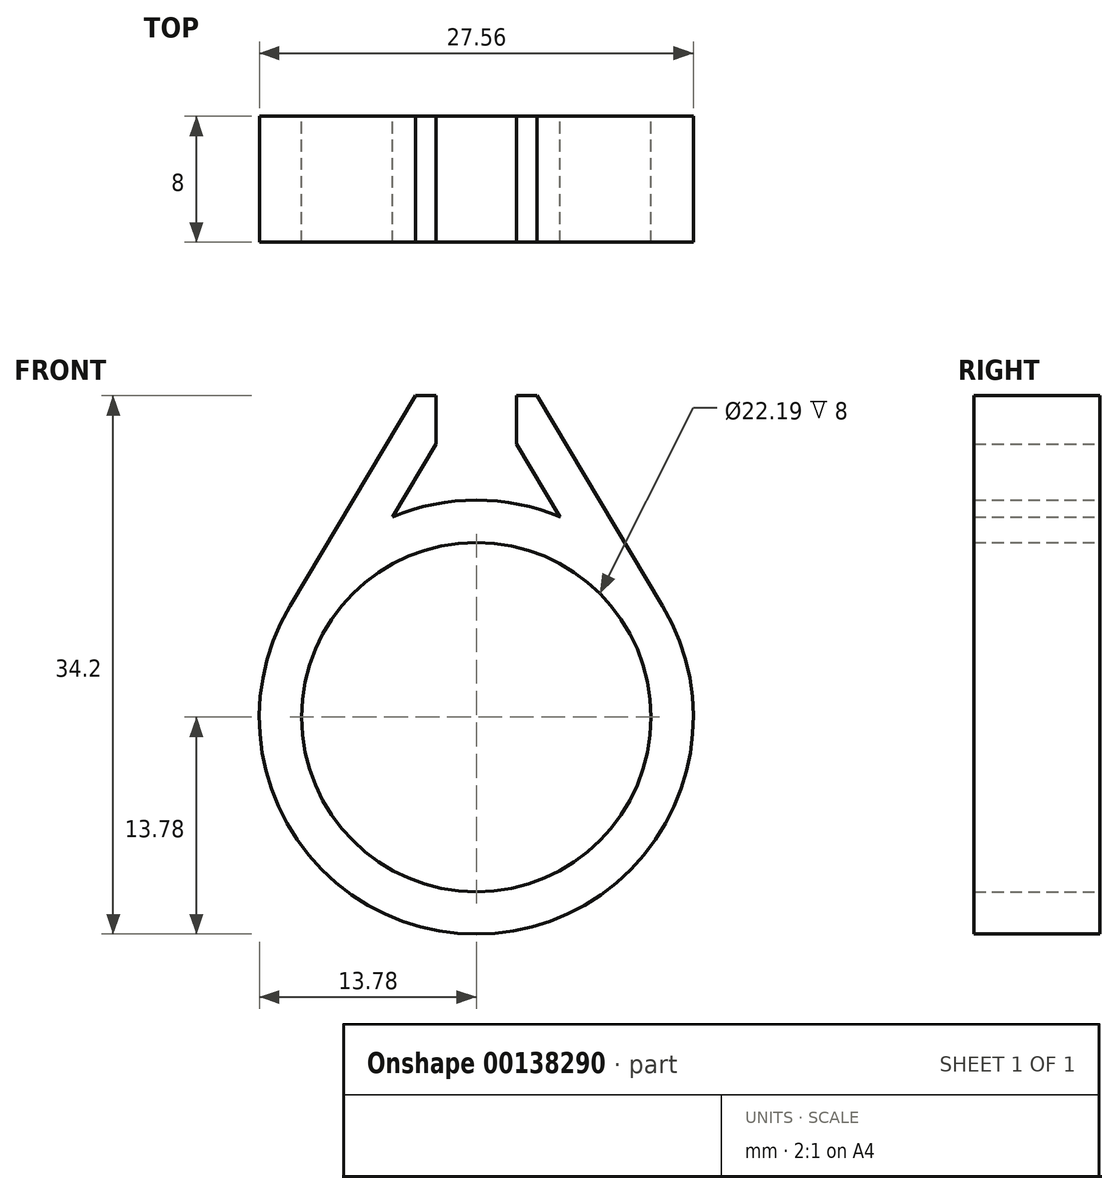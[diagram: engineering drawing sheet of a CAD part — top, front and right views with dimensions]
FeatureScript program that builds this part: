
annotation { "Feature Type Name" : "Feature", "Feature Type Description" : "" }
export const myFeature = defineFeature(function(context is Context, id is Id, definition is map)
    precondition{}
    {
        {
            var Q0;
            Q0=qCreatedBy(makeId("Front.planeOp"),FACE);
            var sketch = newSketch(context, id + "F0", { "sketchPlane" : qUnion([Q0])});
            skCircle(sketch, "E0", {"center": v(0, 0) * mm, "radius": 11.1 * mm});
            skCircle(sketch, "E1", {"center": v(0, 0) * mm, "radius": 13.78 * mm});
            skLineSegment(sketch, "E2.left", {"start": v(-2.56, 22.6) * mm, "end": v(-2.56, 17.72) * mm});
            skLineSegment(sketch, "E2.right", {"start": v(2.84, 22.6) * mm, "end": v(2.84, 17.22) * mm});
            skLineSegment(sketch, "E3", {"start": v(-2.56, 22.6) * mm, "end": v(-11.83, 7.07) * mm});
            skLineSegment(sketch, "E4", {"start": v(2.84, 22.6) * mm, "end": v(11.83, 7.07) * mm});
            skPoint(sketch, "E5.startSnap0", {"position": v(-7.2, 14.83) * mm});
            skPoint(sketch, "E6.endSnap0", {"position": v(7.34, 14.83) * mm});
            skPoint(sketch, "E7.orphan", {"position": v(-2.56, 25.36) * mm});
            skPoint(sketch, "E8.orphan", {"position": v(2.84, 24.86) * mm});
            skPoint(sketch, "E2.top.end.orphan", {"position": v(2.56, -25.36) * mm});
            skPoint(sketch, "E2.top.start.orphan", {"position": v(-2.84, -24.86) * mm});
            skPoint(sketch, "E5.start.orphan", {"position": v(-7.2, 11.75) * mm});
            skPoint(sketch, "E6.end.orphan", {"position": v(7.34, 12.29) * mm});
            skLineSegment(sketch, "E9", {"start": v(-2.56, 17.35) * mm, "end": v(-5.33, 12.71) * mm});
            skLineSegment(sketch, "E10", {"start": v(-5.33, 12.71) * mm, "end": v(-2.56, 17.35) * mm});
            skLineSegment(sketch, "E11", {"start": v(-2.56, 17.72) * mm, "end": v(-2.56, 17.35) * mm});
            skLineSegment(sketch, "E12.MirrorCS", {"start": v(2.56, 22.6) * mm, "end": v(2.56, 17.72) * mm});
            skLineSegment(sketch, "E13.MirrorCS", {"start": v(5.33, 12.71) * mm, "end": v(2.56, 17.35) * mm});
            skLineSegment(sketch, "E14.MirrorCS", {"start": v(2.56, 22.6) * mm, "end": v(11.83, 7.07) * mm});
            skLineSegment(sketch, "E15.MirrorCS", {"start": v(2.56, 17.72) * mm, "end": v(2.56, 17.35) * mm});
            skSolve(sketch);
        }
        {
            var Q0;
            Q0 = qSketchRegion(id + "F0", true);
            extrude(context, id + "F1", {"entities" : qUnion([Q0]), "depth" : 8 * mm});
        }
        {
            var Q0;
            Q0=makeQuery(id+"F1.opExtrude","CAP_FACE",FACE,{"disambiguationData":[OSD([sQuery(id+"F0.wireOp",EDGE,"E0"),sQuery(id+"F0.wireOp",EDGE,"E2.left"),sQuery(id+"F0.wireOp",EDGE,"E3"),sQuery(id+"F0.wireOp",EDGE,"E10"),sQuery(id+"F0.wireOp",EDGE,"E11"),sQuery(id+"F0.wireOp",EDGE,"E12.MirrorCS"),sQuery(id+"F0.wireOp",EDGE,"E13.MirrorCS"),sQuery(id+"F0.wireOp",EDGE,"E14.MirrorCS"),sQuery(id+"F0.wireOp",EDGE,"E1"),sQuery(id+"F0.wireOp",EDGE,"E15.MirrorCS")])],"isStart":false});
            var sketch = newSketch(context, id + "F2", { "sketchPlane" : qUnion([Q0])});
            skLineSegment(sketch, "E16.bottom", {"start": v(-6.74, 20.42) * mm, "end": v(10.76, 20.42) * mm});
            skLineSegment(sketch, "E16.top", {"start": v(-6.74, 23.38) * mm, "end": v(10.76, 23.38) * mm});
            skLineSegment(sketch, "E16.left", {"start": v(-6.74, 20.42) * mm, "end": v(-6.74, 23.38) * mm});
            skLineSegment(sketch, "E16.right", {"start": v(10.76, 20.42) * mm, "end": v(10.76, 23.38) * mm});
            skSolve(sketch);
        }
        {
            var Q0;
            {var subQ0=sQuery(id+"F2.wireOp",EDGE,"E16.bottom");var subQ1=makeQuery(id+"F1.opExtrude","CAP_EDGE",EDGE,{"disambiguationData":[OSD([sQuery(id+"F0.wireOp",EDGE,"E14.MirrorCS")])],"isStart":false});var subQ2=makeQuery(id+"F2.imprint","INTERSECT",VERTEX,{"derivedFrom":[subQ1,subQ0]});Q0=makeQuery(id+"F2.imprint","IMPRINT",FACE,{"disambiguationData":[TD([[makeQuery(id+"F2.imprint","IMPRINT",EDGE,{"disambiguationData":[TD([[subQ2,1.0]])],"derivedFrom":subQ0}),1.0]])]});}
            var Q1;
            {var subQ0=sQuery(id+"F2.wireOp",EDGE,"E16.bottom");var subQ1=makeQuery(id+"F1.opExtrude","CAP_EDGE",EDGE,{"disambiguationData":[OSD([sQuery(id+"F0.wireOp",EDGE,"E3")])],"isStart":false});var subQ2=makeQuery(id+"F2.imprint","INTERSECT",VERTEX,{"derivedFrom":[subQ1,subQ0]});Q1=makeQuery(id+"F2.imprint","IMPRINT",FACE,{"disambiguationData":[TD([[makeQuery(id+"F2.imprint","IMPRINT",EDGE,{"disambiguationData":[TD([[subQ2,-1.0]])],"derivedFrom":subQ0}),1.0]])]});}
            extrude(context, id + "F3", {"entities" : qUnion([Q0, Q1]), "operationType" : NewBodyOperationType.REMOVE, "endBound" : BoundingType.THROUGH_ALL, "oppositeDirection" : true, "depth" : 25 * mm});
        }
    });
